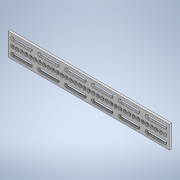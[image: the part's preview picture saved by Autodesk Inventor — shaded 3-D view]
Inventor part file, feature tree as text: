
AUTODESK INVENTOR PART (.ipt)
format: ipt  version: 2020 (Build 240168000, 168)  size: 242,176 bytes
history: native  units: in
note: dims shown in document units (in); Inventor stores cm internally (conversion verified against a paired STEP export)
features: extrude x1, sketch x1
ambient origin geometry x8: Origin, YZ Plane, XZ Plane, XY Plane, X Axis, Y Axis, Z Axis, Center Point
bodies: Solid1 (feature_tree)
feature tree (2):
  extrude  "Extrusion1"  Depth=1.25in
  sketch  "Sketch1"  dims[d0=9.0in d1=1.25in d2=0.101in d3=1.0in d4=0.25in d5=0.25in d6=2.3622in d8=1.5in d9=0.7874in d11=0.75in d14=0.25in d15=13.7795in d17=0.25in d18=0.3937in d20=1.0in d22=0.196in d23=0.125in d24=0.0in]
